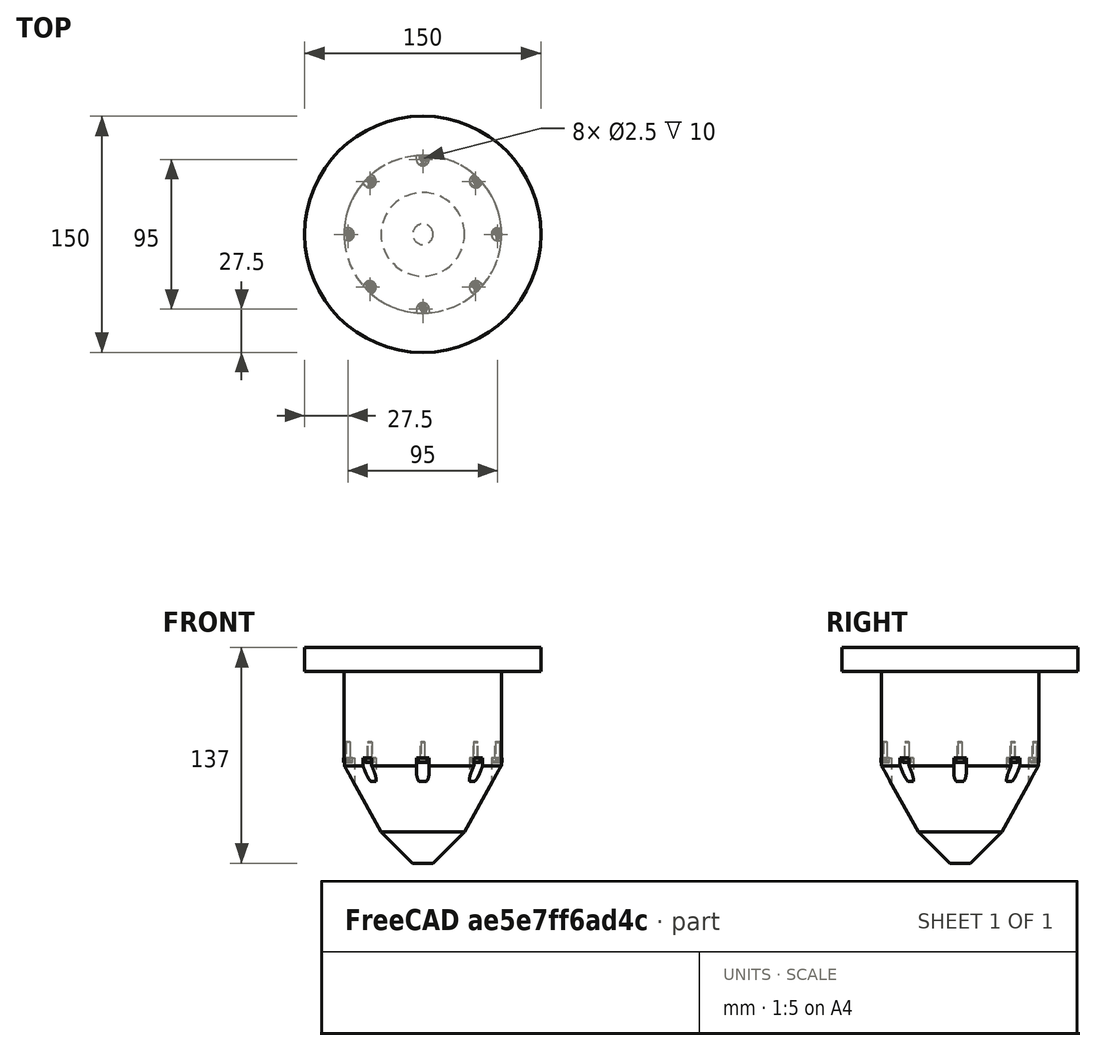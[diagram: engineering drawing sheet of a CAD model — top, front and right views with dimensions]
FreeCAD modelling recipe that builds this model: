
FCSTD DOCUMENT  (FreeCAD 0.20R)
Label: XL30ColumnOutline
License: All rights reserved
LicenseURL: http://en.wikipedia.org/wiki/All_rights_reserved
objects: Part::Cylinder×18, Part::Compound×17, Part::MultiFuse×11, Part::Box×8, Part::FeaturePython×8, Part::Cone×2, Part::Cut×2
note: 66 computed .brp shape members not serialized (recipe doc carries the construction recipe); baked Part::Feature solids carry a one-line shape summary decoded from their .brp

FEATURE [Part::Cylinder] Cylinder
  Angle = 360
  AttacherType = Attacher::AttachEngine3D
  FirstAngle = 0
  Height = 15
  Placement = pos=(0,0,20) rot=(0,0,1;0rad)
  Radius = 75
  SecondAngle = 0
FEATURE [Part::Cylinder] Cylinder001
  Angle = 360
  AttacherType = Attacher::AttachEngine3D
  FirstAngle = 0
  Height = 60
  Placement = pos=(0,0,-40) rot=(0,0,1;0rad)
  Radius = 50
  SecondAngle = 0
FEATURE [Part::Cone] Cone
  Angle = 360
  AttacherType = Attacher::AttachEngine3D
  Height = 42
  Placement = pos=(0,0,-82) rot=(0,0,1;0rad)
  Radius1 = 26.5
  Radius2 = 50
FEATURE [Part::Cone] Cone001
  Angle = 360
  AttacherType = Attacher::AttachEngine3D
  Height = 20
  Placement = pos=(0,0,-102) rot=(0,0,1;0rad)
  Radius1 = 6.5
  Radius2 = 26.5
FEATURE [Part::MultiFuse] Fusion  label="OuterShell"
  Shapes = -> [Cylinder,Cylinder001,Cone,Cone001]
FEATURE [Part::Cylinder] Cylinder002
  Angle = 360
  AttacherType = Attacher::AttachEngine3D
  FirstAngle = 0
  Height = 15
  Placement = pos=(47.5,0,0) rot=(0,0,1;0rad)
  Radius = 4
  SecondAngle = 0
FEATURE [Part::Box] Box  label="Cube"
  AttacherType = Attacher::AttachEngine3D
  Height = 15
  Length = 10
  Placement = pos=(47.5,-4,0) rot=(0,0,1;0rad)
  Width = 8
FEATURE [Part::MultiFuse] Fusion001
  Shapes = -> [Cylinder002,Box]
FEATURE [Part::Box] Box001  label="Cube001"
  AttacherType = Attacher::AttachEngine3D
  Height = 15
  Length = 10
  Placement = pos=(47.5,-4,0) rot=(0,0,1;0rad)
  Width = 8
FEATURE [Part::Cylinder] Cylinder003
  Angle = 360
  AttacherType = Attacher::AttachEngine3D
  FirstAngle = 0
  Height = 15
  Placement = pos=(47.5,0,0) rot=(0,0,1;0rad)
  Radius = 4
  SecondAngle = 0
FEATURE [Part::MultiFuse] Fusion002
  Placement = pos=(0,0,0) rot=(0,0,1;0.785398rad)
  Shapes = -> [Cylinder003,Box001]
FEATURE [Part::Box] Box002  label="Cube002"
  AttacherType = Attacher::AttachEngine3D
  Height = 15
  Length = 10
  Placement = pos=(47.5,-4,0) rot=(0,0,1;0rad)
  Width = 8
FEATURE [Part::Cylinder] Cylinder004
  Angle = 360
  AttacherType = Attacher::AttachEngine3D
  FirstAngle = 0
  Height = 15
  Placement = pos=(47.5,0,0) rot=(0,0,1;0rad)
  Radius = 4
  SecondAngle = 0
FEATURE [Part::MultiFuse] Fusion003
  Placement = pos=(0,0,0) rot=(0,0,1;1.5708rad)
  Shapes = -> [Cylinder004,Box002]
FEATURE [Part::Box] Box003  label="Cube003"
  AttacherType = Attacher::AttachEngine3D
  Height = 15
  Length = 10
  Placement = pos=(47.5,-4,0) rot=(0,0,1;0rad)
  Width = 8
FEATURE [Part::Cylinder] Cylinder005
  Angle = 360
  AttacherType = Attacher::AttachEngine3D
  FirstAngle = 0
  Height = 15
  Placement = pos=(47.5,0,0) rot=(0,0,1;0rad)
  Radius = 4
  SecondAngle = 0
FEATURE [Part::MultiFuse] Fusion004
  Placement = pos=(0,0,0) rot=(0,0,1;2.35619rad)
  Shapes = -> [Cylinder005,Box003]
FEATURE [Part::Box] Box004  label="Cube004"
  AttacherType = Attacher::AttachEngine3D
  Height = 15
  Length = 10
  Placement = pos=(47.5,-4,0) rot=(0,0,1;0rad)
  Width = 8
FEATURE [Part::Cylinder] Cylinder006
  Angle = 360
  AttacherType = Attacher::AttachEngine3D
  FirstAngle = 0
  Height = 15
  Placement = pos=(47.5,0,0) rot=(0,0,1;0rad)
  Radius = 4
  SecondAngle = 0
FEATURE [Part::MultiFuse] Fusion005
  Placement = pos=(0,0,0) rot=(0,0,1;3.14159rad)
  Shapes = -> [Cylinder006,Box004]
FEATURE [Part::Box] Box005  label="Cube005"
  AttacherType = Attacher::AttachEngine3D
  Height = 15
  Length = 10
  Placement = pos=(47.5,-4,0) rot=(0,0,1;0rad)
  Width = 8
FEATURE [Part::Cylinder] Cylinder007
  Angle = 360
  AttacherType = Attacher::AttachEngine3D
  FirstAngle = 0
  Height = 15
  Placement = pos=(47.5,0,0) rot=(0,0,1;0rad)
  Radius = 4
  SecondAngle = 0
FEATURE [Part::MultiFuse] Fusion006
  Placement = pos=(0,0,0) rot=(0,0,1;3.92699rad)
  Shapes = -> [Cylinder007,Box005]
FEATURE [Part::Box] Box006  label="Cube006"
  AttacherType = Attacher::AttachEngine3D
  Height = 15
  Length = 10
  Placement = pos=(47.5,-4,0) rot=(0,0,1;0rad)
  Width = 8
FEATURE [Part::Cylinder] Cylinder008
  Angle = 360
  AttacherType = Attacher::AttachEngine3D
  FirstAngle = 0
  Height = 15
  Placement = pos=(47.5,0,0) rot=(0,0,1;0rad)
  Radius = 4
  SecondAngle = 0
FEATURE [Part::MultiFuse] Fusion007
  Placement = pos=(0,0,0) rot=(0,0,1;4.71239rad)
  Shapes = -> [Cylinder008,Box006]
FEATURE [Part::Box] Box007  label="Cube007"
  AttacherType = Attacher::AttachEngine3D
  Height = 15
  Length = 10
  Placement = pos=(47.5,-4,0) rot=(0,0,1;0rad)
  Width = 8
FEATURE [Part::Cylinder] Cylinder009
  Angle = 360
  AttacherType = Attacher::AttachEngine3D
  FirstAngle = 0
  Height = 15
  Placement = pos=(47.5,0,0) rot=(0,0,1;0rad)
  Radius = 4
  SecondAngle = 0
FEATURE [Part::MultiFuse] Fusion008
  Placement = pos=(0,0,0) rot=(0,0,1;5.49779rad)
  Shapes = -> [Cylinder009,Box007]
FEATURE [Part::MultiFuse] Fusion009  label="CutsForScrews"
  Placement = pos=(0,0,-50) rot=(0,0,1;0rad)
  Shapes = -> [Fusion008,Fusion001,Fusion002,Fusion003,Fusion004,Fusion005,Fusion006,Fusion007]
FEATURE [Part::Cut] Cut
  Base = -> Fusion
  Tool = -> Fusion009
FEATURE [Part::Cylinder] Cylinder017
  Angle = 360
  AttacherType = Attacher::AttachEngine3D
  FirstAngle = 0
  Height = 10
  Placement = pos=(47.5,0,0) rot=(0,0,1;5.49779rad)
  Radius = 1.25
  SecondAngle = 0
FEATURE [Part::Compound] Compound
  Links = -> [Cylinder017]
FEATURE [Part::Cylinder] Cylinder018
  Angle = 360
  AttacherType = Attacher::AttachEngine3D
  FirstAngle = 0
  Height = 10
  Placement = pos=(47.5,0,0) rot=(0,0,-1;0.785398rad)
  Radius = 1.25
  SecondAngle = 0
FEATURE [Part::Compound] Compound001
  Links = -> [Cylinder018]
  Placement = pos=(0,0,0) rot=(0,0,1;0.785398rad)
FEATURE [Part::Cylinder] Cylinder019
  Angle = 360
  AttacherType = Attacher::AttachEngine3D
  FirstAngle = 0
  Height = 10
  Placement = pos=(47.5,0,0) rot=(0,0,-1;0.785398rad)
  Radius = 1.25
  SecondAngle = 0
FEATURE [Part::Compound] Compound002
  Links = -> [Cylinder019]
  Placement = pos=(0,0,0) rot=(0,0,1;1.5708rad)
FEATURE [Part::Cylinder] Cylinder020
  Angle = 360
  AttacherType = Attacher::AttachEngine3D
  FirstAngle = 0
  Height = 10
  Placement = pos=(47.5,0,0) rot=(0,0,-1;0.785398rad)
  Radius = 1.25
  SecondAngle = 0
FEATURE [Part::Compound] Compound003
  Links = -> [Cylinder020]
  Placement = pos=(0,0,0) rot=(0,0,1;2.35619rad)
FEATURE [Part::Cylinder] Cylinder021
  Angle = 360
  AttacherType = Attacher::AttachEngine3D
  FirstAngle = 0
  Height = 10
  Placement = pos=(47.5,0,0) rot=(0,0,-1;0.785398rad)
  Radius = 1.25
  SecondAngle = 0
FEATURE [Part::Compound] Compound004
  Links = -> [Cylinder021]
  Placement = pos=(0,0,0) rot=(0,0,1;3.14159rad)
FEATURE [Part::Cylinder] Cylinder022
  Angle = 360
  AttacherType = Attacher::AttachEngine3D
  FirstAngle = 0
  Height = 10
  Placement = pos=(47.5,0,0) rot=(0,0,-1;0.785398rad)
  Radius = 1.25
  SecondAngle = 0
FEATURE [Part::Compound] Compound005
  Links = -> [Cylinder022]
  Placement = pos=(0,0,0) rot=(0,0,1;3.92699rad)
FEATURE [Part::Cylinder] Cylinder023
  Angle = 360
  AttacherType = Attacher::AttachEngine3D
  FirstAngle = 0
  Height = 10
  Placement = pos=(47.5,0,0) rot=(0,0,-1;0.785398rad)
  Radius = 1.25
  SecondAngle = 0
FEATURE [Part::Compound] Compound006
  Links = -> [Cylinder023]
  Placement = pos=(0,0,0) rot=(0,0,1;4.71239rad)
FEATURE [Part::Cylinder] Cylinder024
  Angle = 360
  AttacherType = Attacher::AttachEngine3D
  FirstAngle = 0
  Height = 10
  Placement = pos=(47.5,0,0) rot=(0,0,-1;0.785398rad)
  Radius = 1.25
  SecondAngle = 0
FEATURE [Part::Compound] Compound007
  Links = -> [Cylinder024]
  Placement = pos=(0,0,0) rot=(0,0,1;5.49779rad)
FEATURE [Part::MultiFuse] Fusion010  label="M3x10DrillHoles"
  Placement = pos=(0,0,-35) rot=(0,0,1;0rad)
  Shapes = -> [Compound007,Compound,Compound001,Compound002,Compound003,Compound004,Compound005,Compound006]
FEATURE [Part::Cut] Cut001  label="BasicOutline_Part0and1"
  Base = -> Cut
  Tool = -> Fusion010
FEATURE [Part::FeaturePython] Screw  label="M3x10-Screw"  # Fasteners workbench fastener (typed FeaturePython)
  Placement = pos=(47.5,0,0) rot=(0,1,0;3.14159rad)
  diameter = 4
  invert = false
  leftHanded = false
  length = 3
  lengthCustom = 10
  matchOuter = false
  offset = 0
  thread = false
  type = 48
FEATURE [Part::Compound] Compound008
  Links = -> [Screw]
FEATURE [Part::FeaturePython] Screw001  label="M3x10-Screw001"  # Fasteners workbench fastener (typed FeaturePython)
  Placement = pos=(47.5,0,0) rot=(0,1,0;3.14159rad)
  diameter = 4
  invert = false
  leftHanded = false
  length = 3
  lengthCustom = 10
  matchOuter = false
  offset = 0
  thread = false
  type = 48
FEATURE [Part::Compound] Compound009
  Links = -> [Screw001]
  Placement = pos=(0,0,0) rot=(0,0,1;0.785398rad)
FEATURE [Part::FeaturePython] Screw002  label="M3x10-Screw002"  # Fasteners workbench fastener (typed FeaturePython)
  Placement = pos=(47.5,0,0) rot=(0,1,0;3.14159rad)
  diameter = 4
  invert = false
  leftHanded = false
  length = 3
  lengthCustom = 10
  matchOuter = false
  offset = 0
  thread = false
  type = 48
FEATURE [Part::Compound] Compound010
  Links = -> [Screw002]
  Placement = pos=(0,0,0) rot=(0,0,1;1.5708rad)
FEATURE [Part::FeaturePython] Screw003  label="M3x10-Screw003"  # Fasteners workbench fastener (typed FeaturePython)
  Placement = pos=(47.5,0,0) rot=(0,1,0;3.14159rad)
  diameter = 4
  invert = false
  leftHanded = false
  length = 3
  lengthCustom = 10
  matchOuter = false
  offset = 0
  thread = false
  type = 48
FEATURE [Part::Compound] Compound011
  Links = -> [Screw003]
  Placement = pos=(0,0,0) rot=(0,0,1;2.35619rad)
FEATURE [Part::FeaturePython] Screw004  label="M3x10-Screw004"  # Fasteners workbench fastener (typed FeaturePython)
  Placement = pos=(47.5,0,0) rot=(0,1,0;3.14159rad)
  diameter = 4
  invert = false
  leftHanded = false
  length = 3
  lengthCustom = 10
  matchOuter = false
  offset = 0
  thread = false
  type = 48
FEATURE [Part::Compound] Compound012
  Links = -> [Screw004]
  Placement = pos=(0,0,0) rot=(0,0,1;3.14159rad)
FEATURE [Part::FeaturePython] Screw005  label="M3x10-Screw005"  # Fasteners workbench fastener (typed FeaturePython)
  Placement = pos=(47.5,0,0) rot=(0,1,0;3.14159rad)
  diameter = 4
  invert = false
  leftHanded = false
  length = 3
  lengthCustom = 10
  matchOuter = false
  offset = 0
  thread = false
  type = 48
FEATURE [Part::Compound] Compound013
  Links = -> [Screw005]
  Placement = pos=(0,0,0) rot=(0,0,1;3.92699rad)
FEATURE [Part::FeaturePython] Screw006  label="M3x10-Screw006"  # Fasteners workbench fastener (typed FeaturePython)
  Placement = pos=(47.5,0,0) rot=(0,1,0;3.14159rad)
  diameter = 4
  invert = false
  leftHanded = false
  length = 3
  lengthCustom = 10
  matchOuter = false
  offset = 0
  thread = false
  type = 48
FEATURE [Part::Compound] Compound014
  Links = -> [Screw006]
  Placement = pos=(0,0,0) rot=(0,0,1;4.71239rad)
FEATURE [Part::FeaturePython] Screw007  label="M3x10-Screw007"  # Fasteners workbench fastener (typed FeaturePython)
  Placement = pos=(47.5,0,0) rot=(0,1,0;3.14159rad)
  diameter = 4
  invert = false
  leftHanded = false
  length = 3
  lengthCustom = 10
  matchOuter = false
  offset = 0
  thread = false
  type = 48
FEATURE [Part::Compound] Compound015
  Links = -> [Screw007]
  Placement = pos=(0,0,0) rot=(0,0,1;5.49779rad)
FEATURE [Part::Compound] Compound016  label="8xM3x10"
  Links = -> [Compound015,Compound008,Compound009,Compound010,Compound011,Compound012,Compound013,Compound014]
  Placement = pos=(0,0,-35) rot=(0,0,1;0rad)
